# Revit family: a64a3d83_e24b_42b4_88e5_11b3e33cae8f
name_source: partatom
category: Generic Models
revit_build: Autodesk Revit Architecture 2015 (Build: 20140606_1530(x64)
units: mm (PartAtom-declared; Revit-internal decimal feet)

## types (1)
- Default
    BIMobject category = Outdoor Furniture
    BOSUseNativeGeometries = 1
    Date of publishing = 9/1/2012
    Design country = Sweden
    Edition number = 1
    IFC Classification = Furniture
    Installation instructions = http://www.hags.com
    Manufacturer country = Sweden
    Manufacturer name = Hags
    Material main = Wood
    Material secondary = Plastic
    NBS Reference Code = 31-61
    NBS Reference Description = Play Equipment
    Nominal height = 6000
    Nominal width = 8400
    Product Guid = d577eca0-4609-4367-a07b-63190270d2fe
    Product SKU = 8008258
    Product data url = https://bimobject.com
    Product family = Outdoor Furniture
    Product group = Play Structure
    Product name = Active 6000
    QR code = http://bimobject.com
    UNSPSC Code = 301036
    Uniclass 1.4 Code = JN
    Uniclass 1.4 Description = Furniture/Equipment
    Uniclass 2.0 Code = PR-31-61
    Uniclass 2.0 Description = Play Equipment
    Weight Net (Kg) = 315

## geometry (parser evidence)
native form markers: Sweep x2
no freeform markers — native parametric forms only
